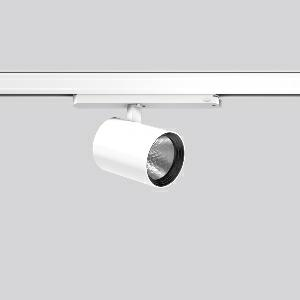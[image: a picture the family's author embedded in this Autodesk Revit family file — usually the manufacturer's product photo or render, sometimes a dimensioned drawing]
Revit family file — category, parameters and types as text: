
# Revit family: deecos_s_mini_track-in_742258_002_730_dd90
name_source: partatom
category: Lighting Fixtures
units: mm (PartAtom-declared; Revit-internal decimal feet)

## family parameters
Cut with Voids When Loaded = No
Host = Face
Light Source = No
Part Type = Normal
Room Calculation Point = No
Round Connector Dimension = Use Diameter
Shared = No

## types (1)
- DEECOS S mini track-in (1 x LED Modul 930, 3550 lm, 3000)
    Apparent Load = 29 VA
    Approval mark = CE
    CIE Flux Codes = 100 100 100 100 100
    Color Rendering = 90
    Color Temperature = 3000
    Default Elevation = 1800 mm
    Description = Series: DEECOS S mini track-in
LED surface-mounted projector in modern design with no visible cooling ribs. Housing: die-cast aluminium, powder-coated. Rotation range: 356°. Swivel range: 90°. Black plastic ring and recessed LED to prevent glare from the side. Optical assembly with reflector made of MIRO-Silver with 98% total light reflection for outstanding efficiency - can be changed without tools. Best colour rendering index Ra>90. With multi adaptor for 3-circuit tracks 230 V. Suitable for Track on ceiling, Wall track. Track-in driver integrated into the adapter. High quality converter without flickering and stroboscopic effect. With Casambi smart+free Bluetooth control for wireless network and operation using Android / iOS devices, free app available for download. The following accessories can be mounted without use of tools: interchangeable lenses, decorative glasses, honeycomb louvre, clear and frosted diffusers, white interchangeable plastic ring. 
Colour: traffic white, matt (RAL 9016)
Diameter: 87 mm
Height: 135 mm
Lamp: LED
Socket: without socket
Colour temperature: 3000K
Colour rendering index (CRI): 92
System power: 29 W
Rated luminous flux: 3550 lm
Luminous efficiency: 122 lm/W
Control gear: Dimmable Bluetooth converter
Protection class: II
Type of protection: IP 20
    Height = 135 mm
    Lamp = 1 x LED Modul 930
    Lamp Light Flux = 3550 lm
    Lamp count = 1
    Length = 87 mm
    Lifetime = 50000 h
    Luminous efficacy = 122 lm/W
    Manufacturer = RZB
    ModVariant = No
    Model = 742258.002.730
    Mounting Place = Ceiling
    Mounting Type = Rail mounted
    Number of Poles = 1
    OnlyDefault = Yes
    Power Factor = 1
    Product Name = DEECOS S mini track-in
    Product group = Track mounted projectors
    ProductGroupID = 301
    Protection Class = Protection class II
    Protection Degree = IP 20
    RLX_Detail_Level = 1
    RLX_Emergency_Light_Flux = 0 lm
    RLX_Emergency_Type = 0
    RLX_Emergency_Type_DB = No
    RlxData = <blob elided: 35069 chars, md5=90c178cf>
    Socket = socket
    Standby Power = 0 W
    System Light Flux = 3550 lm
    System Power = 29 W
    Type Comments = Product without accessories
    Type Image = 742105.002.jpg
    URL = http://relux.com
    VarID = ---
    Voltage = 230 V
    Voltage Range = 220-240 V
    Weight = 0.00 kg
    Width = 0 mm  [stored 0 ft]

note: [stored X ft] marks values corroborated as IEEE doubles in the binary element streams (Revit-internal decimal feet)

## geometry (parser evidence)
native form markers: Blend x4, Sweep x12
no freeform markers — native parametric forms only
